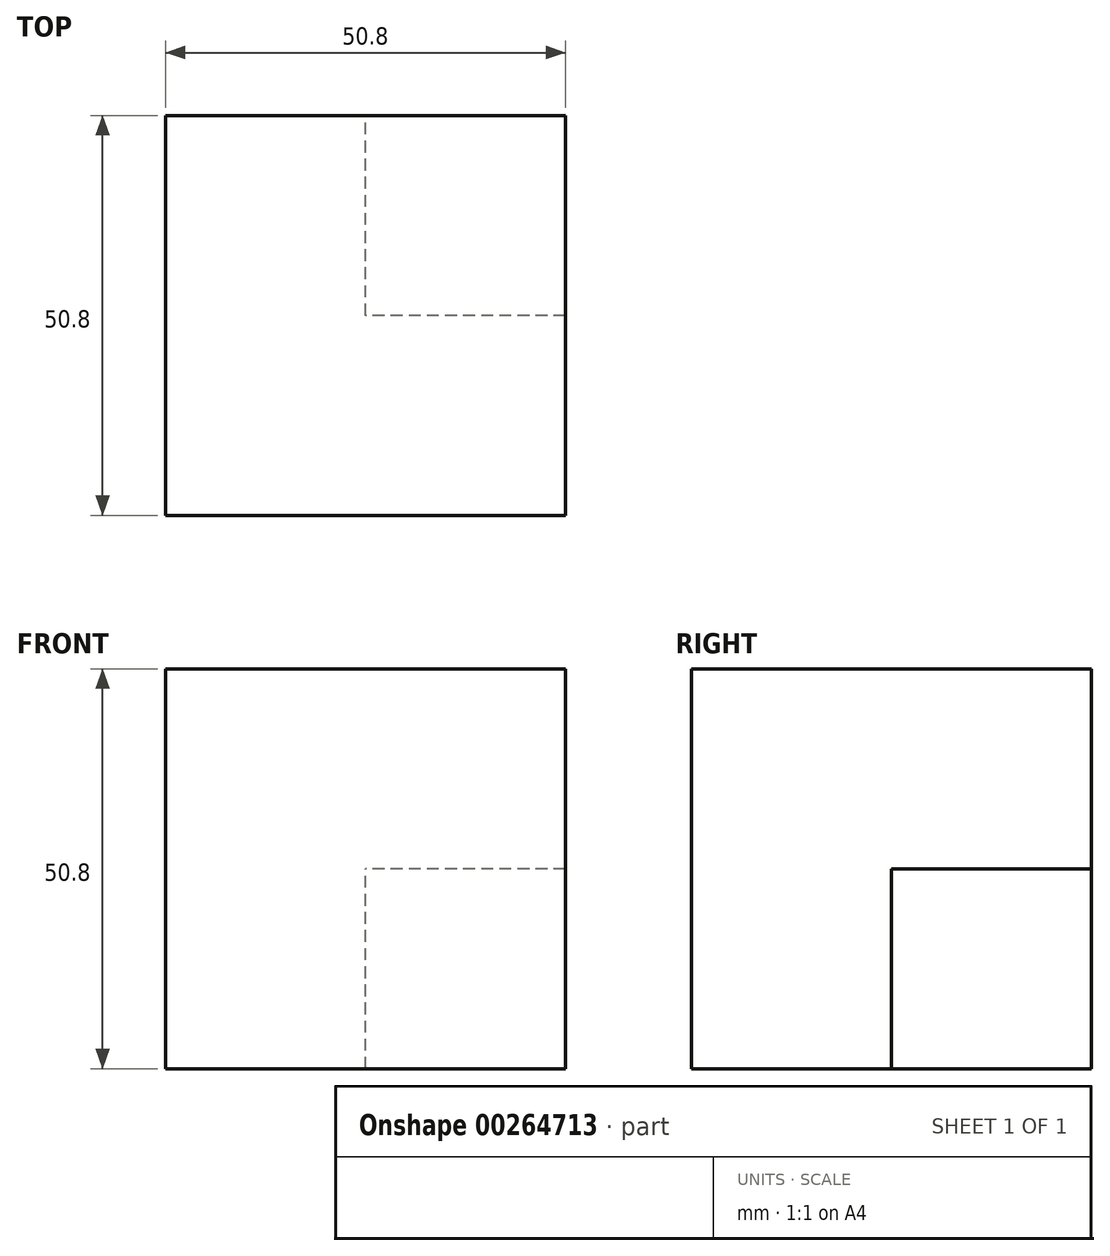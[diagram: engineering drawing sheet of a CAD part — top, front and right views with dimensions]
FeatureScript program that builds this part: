
annotation { "Feature Type Name" : "Feature", "Feature Type Description" : "" }
export const myFeature = defineFeature(function(context is Context, id is Id, definition is map)
    precondition{}
    {
        {
            var Q0;
            Q0=qCreatedBy(makeId("Front.planeOp"),FACE);
            var sketch = newSketch(context, id + "F0", { "sketchPlane" : qUnion([Q0])});
            skLineSegment(sketch, "E0.bottom", {"start": v(0, 0) * mm, "end": v(-50.8, 0) * mm});
            skLineSegment(sketch, "E0.top", {"start": v(0, 50.8) * mm, "end": v(-50.8, 50.8) * mm});
            skLineSegment(sketch, "E0.left", {"start": v(0, 0) * mm, "end": v(0, 50.8) * mm});
            skLineSegment(sketch, "E0.right", {"start": v(-50.8, 0) * mm, "end": v(-50.8, 50.8) * mm});
            skSolve(sketch);
        }
        {
            var Q0;
            Q0 = qSketchRegion(id + "F0", true);
            extrude(context, id + "F1", {"entities" : qUnion([Q0]), "depth" : 50.8 * mm});
        }
        {
            var Q0;
            Q0=qCreatedBy(makeId("Front.planeOp"),FACE);
            var sketch = newSketch(context, id + "F2", { "sketchPlane" : qUnion([Q0])});
            skLineSegment(sketch, "E1.bottom", {"start": v(0, 0) * mm, "end": v(-25.4, 0) * mm});
            skLineSegment(sketch, "E1.top", {"start": v(0, 25.4) * mm, "end": v(-25.4, 25.4) * mm});
            skLineSegment(sketch, "E1.left", {"start": v(0, 0) * mm, "end": v(0, 25.4) * mm});
            skLineSegment(sketch, "E1.right", {"start": v(-25.4, 0) * mm, "end": v(-25.4, 25.4) * mm});
            skSolve(sketch);
        }
        {
            var Q0;
            Q0 = qSketchRegion(id + "F2", true);
            extrude(context, id + "F3", {"entities" : qUnion([Q0]), "operationType" : NewBodyOperationType.REMOVE, "depth" : 25.4 * mm});
        }
    });
